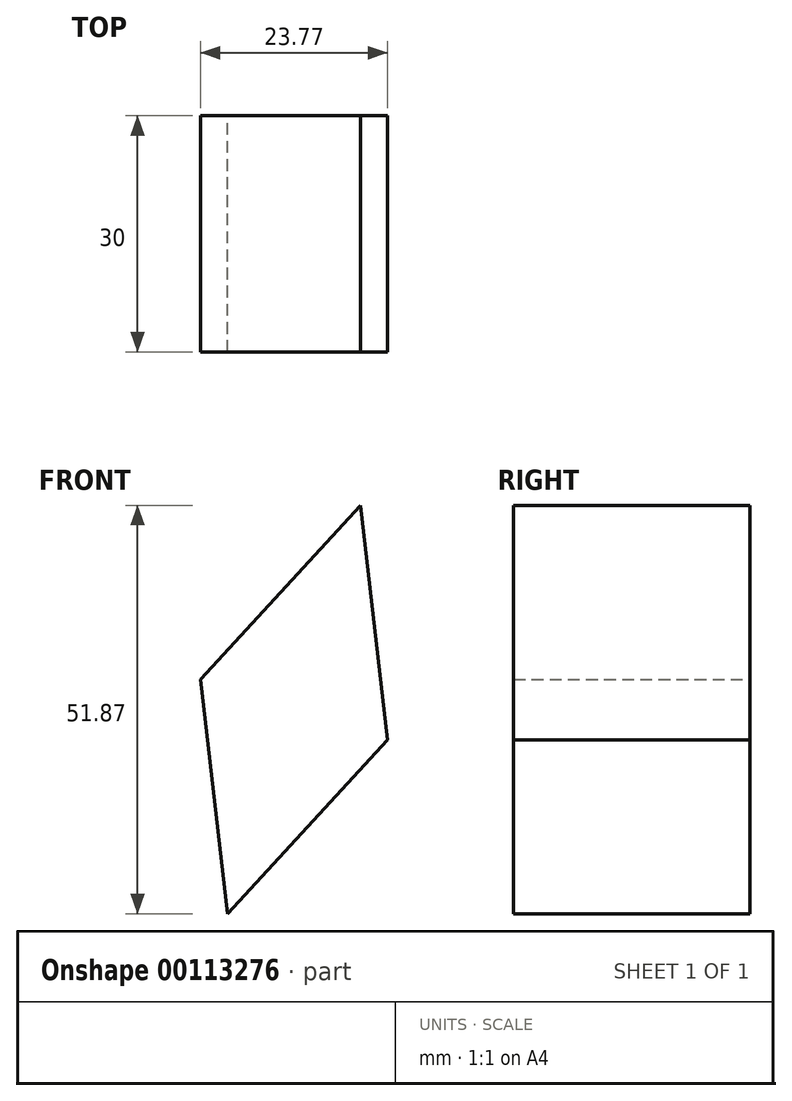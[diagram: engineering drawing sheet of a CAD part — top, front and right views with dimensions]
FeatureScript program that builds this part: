
annotation { "Feature Type Name" : "Feature", "Feature Type Description" : "" }
export const myFeature = defineFeature(function(context is Context, id is Id, definition is map)
    precondition{}
    {
        {
            var Q0;
            Q0=qCreatedBy(makeId("Front.planeOp"),FACE);
            var sketch = newSketch(context, id + "F0", { "sketchPlane" : qUnion([Q0])});
            skLineSegment(sketch, "E0", {"start": v(-9.74, -7.34) * mm, "end": v(-6.28, -37.14) * mm});
            skLineSegment(sketch, "E1", {"start": v(-6.28, -37.14) * mm, "end": v(14.03, -15.07) * mm});
            skLineSegment(sketch, "E2", {"start": v(10.57, 14.73) * mm, "end": v(-9.74, -7.34) * mm});
            skLineSegment(sketch, "E3", {"start": v(10.57, 14.73) * mm, "end": v(14.03, -15.07) * mm});
            skSolve(sketch);
        }
        {
            var Q0;
            Q0=makeQuery(id+"F0.imprint","IMPRINT",FACE,{"disambiguationData":[TD([[makeQuery(id+"F0.imprint","IMPRINT",EDGE,{"derivedFrom":sQuery(id+"F0.wireOp",EDGE,"E0")}),1.0]])]});
            extrude(context, id + "F1", {"entities" : qUnion([Q0]), "depth" : 30 * mm});
        }
    });
